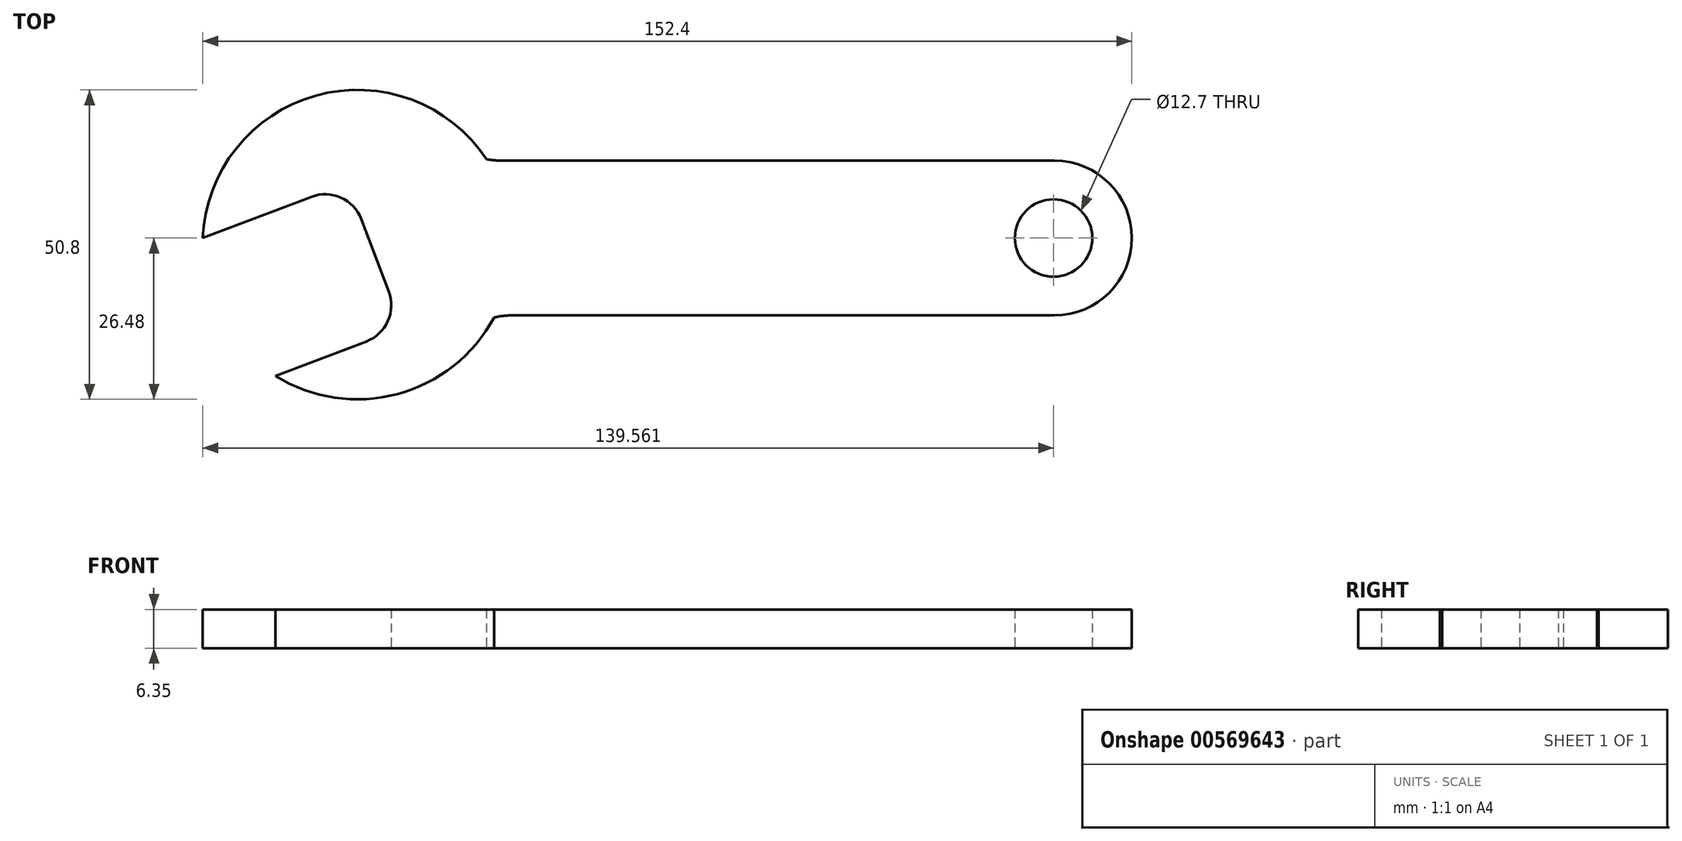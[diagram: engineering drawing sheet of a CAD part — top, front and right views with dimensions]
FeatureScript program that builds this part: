
annotation { "Feature Type Name" : "Feature", "Feature Type Description" : "" }
export const myFeature = defineFeature(function(context is Context, id is Id, definition is map)
    precondition{}
    {
        {
            var Q0;
            Q0=qCreatedBy(makeId("Top.planeOp"),FACE);
            var sketch = newSketch(context, id + "F0", { "sketchPlane" : qUnion([Q0])});
            skLineSegment(sketch, "E0.bottom", {"start": v(50.8, 12.7) * mm, "end": v(-39.8, 12.7) * mm});
            skLineSegment(sketch, "E0.top", {"start": v(50.8, -12.7) * mm, "end": v(-38.1, -12.7) * mm});
            skLineSegment(sketch, "E0.left", {"start": v(63.5, 0) * mm, "end": v(63.5, 0) * mm});
            skLineSegment(sketch, "E0.right", {"start": v(-63.52, 11.62) * mm, "end": v(-63.52, -13.78) * mm});
            skPoint(sketch, "E0.middle", {"position": v(0, 0) * mm});
            skCircle(sketch, "E1", {"center": v(-63.52, -1.08) * mm, "radius": 25.4 * mm});
            skLineSegment(sketch, "E2", {"start": v(-88.9, 0) * mm, "end": v(-71.1, 6.77) * mm});
            skLineSegment(sketch, "E3", {"start": v(-62.9, 3.08) * mm, "end": v(-58.4, -8.79) * mm});
            skLineSegment(sketch, "E4", {"start": v(-62.07, -16.98) * mm, "end": v(-76.96, -22.63) * mm});
            skPoint(sketch, "E5.visualSharp", {"position": v(63.5, 12.7) * mm});
            skArc(sketch, "E5.filletArc", {"start": v(63.5, 0) * mm, "mid": v(59.78, 8.98) * mm, "end": v(50.8, 12.7) * mm});
            skPoint(sketch, "E6.visualSharp", {"position": v(63.5, -12.7) * mm});
            skArc(sketch, "E6.filletArc", {"start": v(50.8, -12.7) * mm, "mid": v(59.78, -8.98) * mm, "end": v(63.5, 0) * mm});
            skPoint(sketch, "E7.visualSharp", {"position": v(-56.14, -14.72) * mm});
            skArc(sketch, "E7.filletArc", {"start": v(-62.07, -16.98) * mm, "mid": v(-58.53, -13.65) * mm, "end": v(-58.4, -8.79) * mm});
            skPoint(sketch, "E8.visualSharp", {"position": v(-65.16, 9.02) * mm});
            skArc(sketch, "E8.filletArc", {"start": v(-62.9, 3.08) * mm, "mid": v(-66.23, 6.62) * mm, "end": v(-71.1, 6.77) * mm});
            skCircle(sketch, "E9", {"center": v(50.66, 0) * mm, "radius": 6.35 * mm});
            skLineSegment(sketch, "E10", {"start": v(-63.52, 11.62) * mm, "end": v(-63.52, 24.32) * mm});
            skLineSegment(sketch, "E11", {"start": v(-63.52, -13.78) * mm, "end": v(-63.52, -26.48) * mm});
            skLineSegment(sketch, "E12", {"start": v(-63.52, -26.48) * mm, "end": v(-44.9, -14.67) * mm});
            skLineSegment(sketch, "E13", {"start": v(-63.52, 24.32) * mm, "end": v(-46.1, 14.37) * mm});
            skPoint(sketch, "E14.newPointB", {"position": v(-63.5, 12.7) * mm});
            skArc(sketch, "E14.filletArc", {"start": v(-46.1, 14.37) * mm, "mid": v(-43.06, 13.13) * mm, "end": v(-39.8, 12.7) * mm});
            skPoint(sketch, "E15.newPointB", {"position": v(-63.5, -12.7) * mm});
            skArc(sketch, "E15.filletArc", {"start": v(-38.1, -12.7) * mm, "mid": v(-41.64, -13.2) * mm, "end": v(-44.9, -14.67) * mm});
            skSolve(sketch);
        }
        {
            var Q0;
            {var subQ4=sQuery(id+"F0.wireOp",EDGE,"E2");Q0=makeQuery(id+"F0.imprint","IMPRINT",FACE,{"disambiguationData":[TD([[makeQuery(id+"F0.imprint","IMPRINT",EDGE,{"derivedFrom":subQ4}),1.0]])]});}
            var Q1;
            {var subQ0=sQuery(id+"F0.wireOp",EDGE,"E4");Q1=makeQuery(id+"F0.imprint","IMPRINT",FACE,{"disambiguationData":[TD([[makeQuery(id+"F0.imprint","IMPRINT",EDGE,{"derivedFrom":subQ0}),1.0]])]});}
            var Q2;
            {var subQ6=sQuery(id+"F0.wireOp",EDGE,"E0.bottom");Q2=makeQuery(id+"F0.imprint","IMPRINT",FACE,{"disambiguationData":[TD([[makeQuery(id+"F0.imprint","IMPRINT",EDGE,{"derivedFrom":subQ6}),1.0]])]});}
            var Q3;
            {var subQ5=sQuery(id+"F0.wireOp",EDGE,"E10");Q3=makeQuery(id+"F0.imprint","IMPRINT",FACE,{"disambiguationData":[TD([[makeQuery(id+"F0.imprint","IMPRINT",EDGE,{"derivedFrom":subQ5}),-1.0]])]});}
            var Q4;
            {var subQ0=sQuery(id+"F0.wireOp",EDGE,"E13");Q4=makeQuery(id+"F0.imprint","IMPRINT",FACE,{"disambiguationData":[TD([[makeQuery(id+"F0.imprint","IMPRINT",EDGE,{"derivedFrom":subQ0}),1.0]])]});}
            var Q5;
            {var subQ0=sQuery(id+"F0.wireOp",EDGE,"E12");Q5=makeQuery(id+"F0.imprint","IMPRINT",FACE,{"disambiguationData":[TD([[makeQuery(id+"F0.imprint","IMPRINT",EDGE,{"derivedFrom":subQ0}),-1.0]])]});}
            extrude(context, id + "F1", {"entities" : qUnion([Q0, Q1, Q2, Q3, Q4, Q5]), "depth" : 6.35 * mm, "offsetDistance" : 25.4 * mm});
        }
    });
